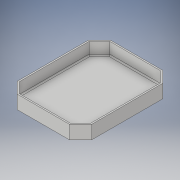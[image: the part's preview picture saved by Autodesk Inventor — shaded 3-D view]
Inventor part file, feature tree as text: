
AUTODESK INVENTOR PART (.ipt)
format: ipt  version: 2017 (Build 210142000, 142)  size: 136,192 bytes
history: native  units: mm
features: extrude x2, other x1, sketch x1, fillet x1
ambient origin geometry x8: Origin, YZ Plane, XZ Plane, XY Plane, X Axis, Y Axis, Z Axis, Center Point
bodies: Body1 (feature_tree)
feature tree (5):
  other  "Твердое тело1"
  sketch  "Эскиз1"
  extrude  "Выдавливание1"  Depth=58.6mm
  extrude  "Выдавливание2"  Depth=74.0mm
  fillet  "Сопряжение1"  Radius=8.5mm
